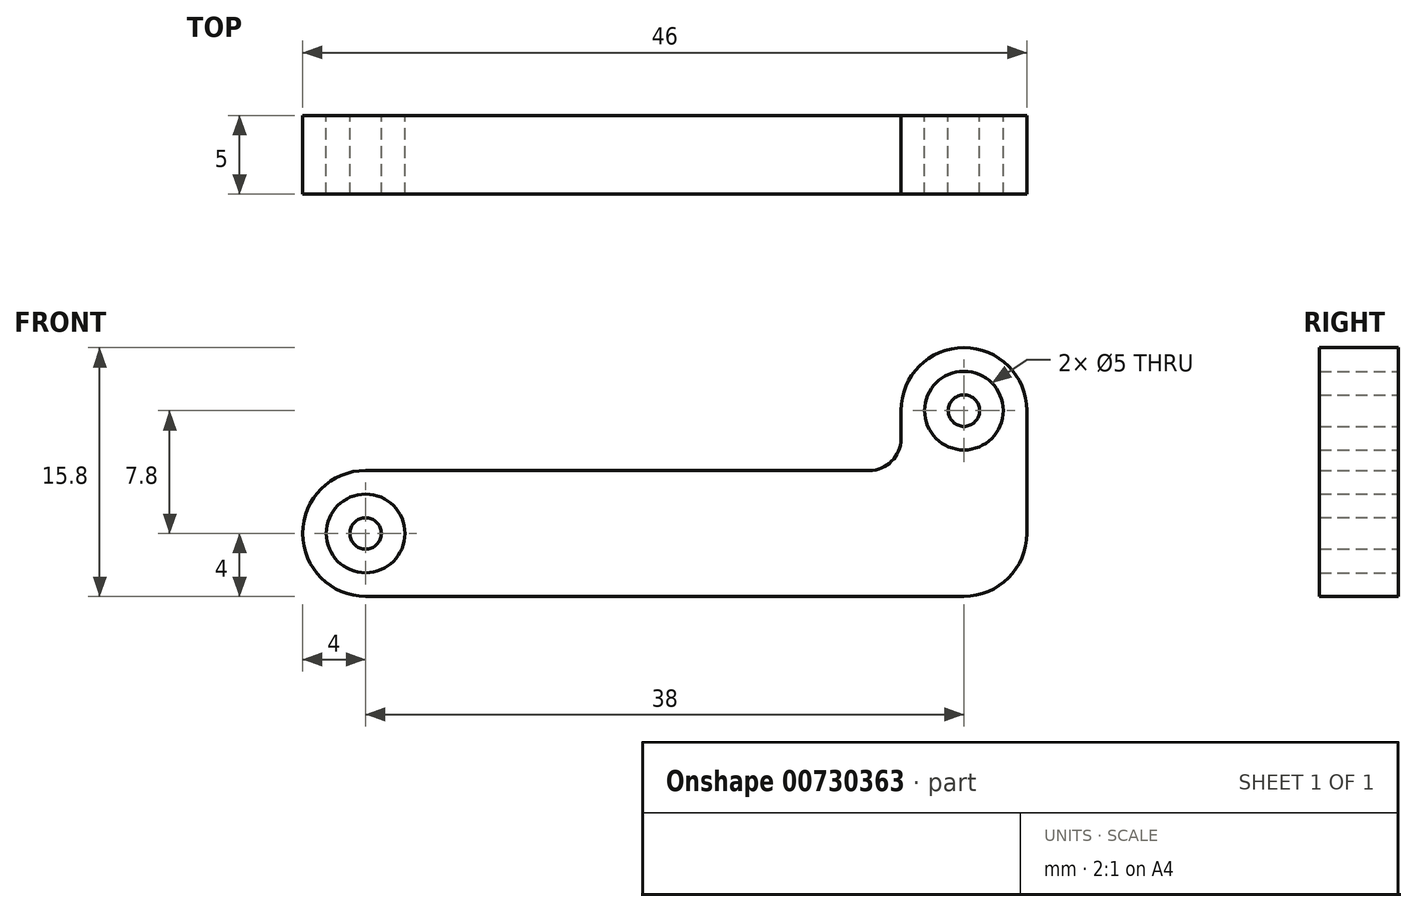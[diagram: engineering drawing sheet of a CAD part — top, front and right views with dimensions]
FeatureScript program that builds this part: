
annotation { "Feature Type Name" : "Feature", "Feature Type Description" : "" }
export const myFeature = defineFeature(function(context is Context, id is Id, definition is map)
    precondition{}
    {
        {
            var Q0;
            Q0=qCreatedBy(makeId("Front.planeOp"),FACE);
            var sketch = newSketch(context, id + "F0", { "sketchPlane" : qUnion([Q0])});
            skArc(sketch, "E0", {"start": v(0, 4) * mm, "mid": v(-4, 0) * mm, "end": v(0, -4) * mm});
            skCircle(sketch, "E1", {"center": v(0, 0) * mm, "radius": 2.5 * mm});
            skCircle(sketch, "E2", {"center": v(0, 0) * mm, "radius": 1 * mm});
            skArc(sketch, "E3", {"start": v(42, 7.8) * mm, "mid": v(38, 11.8) * mm, "end": v(34, 7.8) * mm});
            skCircle(sketch, "E4", {"center": v(38, 7.8) * mm, "radius": 2.5 * mm});
            skCircle(sketch, "E5", {"center": v(38, 7.8) * mm, "radius": 1 * mm});
            skLineSegment(sketch, "E6", {"start": v(0, 4) * mm, "end": v(32, 4) * mm});
            skLineSegment(sketch, "E7.0", {"start": v(0, -4) * mm, "end": v(38, -4) * mm});
            skLineSegment(sketch, "E8", {"start": v(42, 7.8) * mm, "end": v(42, 0) * mm});
            skLineSegment(sketch, "E9", {"start": v(34, 7.8) * mm, "end": v(34, 6) * mm});
            skPoint(sketch, "E10.visualSharp", {"position": v(34, 4) * mm});
            skArc(sketch, "E10.filletArc", {"start": v(32, 4) * mm, "mid": v(33.41, 4.59) * mm, "end": v(34, 6) * mm});
            skPoint(sketch, "E11.visualSharp", {"position": v(42, -4) * mm});
            skArc(sketch, "E11.filletArc", {"start": v(38, -4) * mm, "mid": v(40.83, -2.83) * mm, "end": v(42, 0) * mm});
            skSolve(sketch);
        }
        {
            var Q0;
            Q0 = qSketchRegion(id + "F0", true);
            var Q1;
            Q1=makeQuery(id+"F0.imprint","IMPRINT",FACE,{"disambiguationData":[TD([[makeQuery(id+"F0.imprint","IMPRINT",EDGE,{"derivedFrom":sQuery(id+"F0.wireOp",EDGE,"E2")}),1.0]])]});
            var Q2;
            Q2=makeQuery(id+"F0.imprint","IMPRINT",FACE,{"disambiguationData":[TD([[makeQuery(id+"F0.imprint","IMPRINT",EDGE,{"derivedFrom":sQuery(id+"F0.wireOp",EDGE,"E5")}),1.0]])]});
            extrude(context, id + "F1", {"entities" : qUnion([Q0, Q1, Q2]), "depth" : 5 * mm, "offsetDistance" : 25 * mm});
        }
    });
